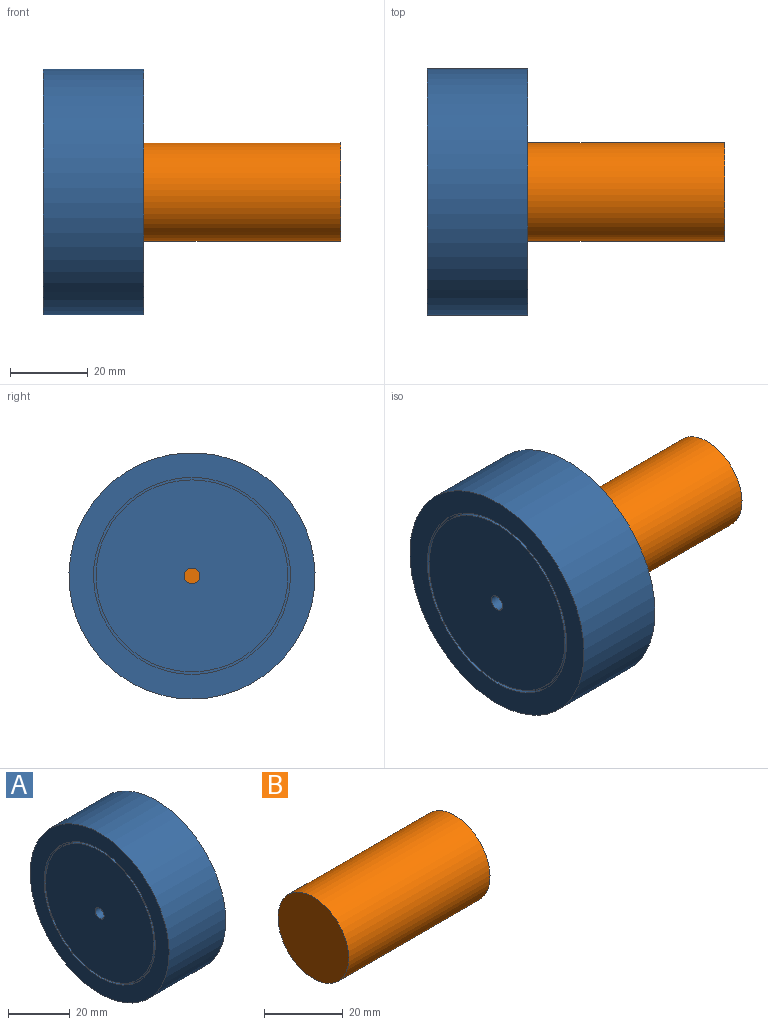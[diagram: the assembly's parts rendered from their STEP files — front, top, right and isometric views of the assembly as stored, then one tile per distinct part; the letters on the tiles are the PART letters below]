
ASSEMBLY  parts=2 mates=1
PART A: 12 faces, bbox 25.9x63.5x63.5 mm
  f0: cylinder r=31.75mm len=63.5mm, axis (-1,0,0), area 5168.4mm2, adj f1,f2
  f1: plane 63.5x63.5mm, normal (1,0,0), area 1488.5mm2, adj f0,f4
  f2: plane 63.5x63.5mm, normal (-1,0,0), area 1140.1mm2, adj f0,f8
  f3: cylinder r=5.74mm len=19.05mm, axis (1,0,0), area 687.1mm2, adj f5,f6
  f4: cylinder r=23.11mm len=46.23mm, axis (1,0,0), area 2766.6mm2, adj f1,f5
  f5: plane 46.23x46.23mm, normal (1,0,0), area 1574.9mm2, adj f3,f4
  f6: plane 11.48x11.48mm, normal (1,0,0), area 90.6mm2, adj f3,f11
  f7: cylinder r=24.77mm len=49.53mm, axis (-1,0,0), area 197.6mm2, adj f9,f10
  f8: cylinder r=25.4mm len=50.8mm, axis (-1,0,0), area 202.7mm2, adj f2,f9
  f9: plane 50.8x50.8mm, normal (-1,0,0), area 100.1mm2, adj f7,f8
  f10: plane 49.53x49.53mm, normal (-1,0,0), area 1913.8mm2, adj f7,f11
  f11: cylinder r=2.03mm len=25.91mm, axis (1,0,0), area 330.8mm2, adj f6,f10
PART B: 3 faces, bbox 50.8x25.4x25.4 mm
  f0: cylinder r=12.7mm len=50.8mm, axis (-1,0,0), area 4053.7mm2, adj f1,f2
  f1: plane 25.4x25.4mm, normal (1,0,0), area 506.7mm2, adj f0
  f2: plane 25.4x25.4mm, normal (-1,0,0), area 506.7mm2, adj f0
PLACE A t=(11.11,-100.24,42.11)mm
PLACE B t=(37.02,-168.56,42.11)mm
MATE fastened A.f0 <-> B.f0  axis (1,0,0) through (37.02,64.11,42.11)mm
